# Revit family: Soap dish-Trendy hotels- Gala -53061
name_source: partatom
category: Plumbing Fixtures
units: mm (PartAtom-declared; Revit-internal decimal feet)

## family parameters
Always vertical = Yes
Cut with Voids When Loaded = No
Host = Wall
OmniClass Number = 23.45.05.00
OmniClass Title = Sanitary Equipment
Part Type = Normal
Room Calculation Point = No
Round Connector Dimension = Use Diameter
Shared = No

## types (1)
- 5306100 Chrome
    BIMobject category = Bathroom Accessories
    Default Elevation = 0 mm  [stored 0 ft]
    Description = Soap dish
    Design country = Spain
    Edition number = 1
    IFC Classification = Object
    Installation instructions = http://www.gala.es
    Manufacturer URL = http://www.gala.es
    Manufacturer country = Spain
    Manufacturer name = GALA
    Nominal height = 0
    Nominal width = 11000
    Primary Material = Chrome-Trendy Hotels-Gala
    Product Guid = 4469e19f-d2f8-4f73-b012-21dce8e6bb21
    Product SKU = 5306100
    Product data url = http://bimobject.com
    Product family = Trendly hotels
    Product group = Bathroom accesories
    QR code = http://bimobject.com
    Technical description = http://www.gala.es
    URL = http://gala.es
    Uniclass 1.4 Code = L824
    Uniclass 1.4 Description = Bathroom, toilet furniture and fittings
    Weight Net (Kg) = 0

note: [stored X ft] marks values corroborated as IEEE doubles in the binary element streams (Revit-internal decimal feet)

## geometry (parser evidence)
native form markers: Sweep x5
no freeform markers — native parametric forms only
